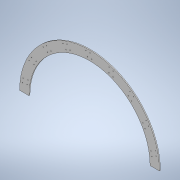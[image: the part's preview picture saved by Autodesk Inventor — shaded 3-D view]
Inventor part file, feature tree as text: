
AUTODESK INVENTOR PART (.ipt)
format: ipt  version: 2020.3 (Build 243373000, 373)  size: 176,640 bytes
history: native  units: mm
features: extrude x3, sketch x3, pattern_circular x1
ambient origin geometry x8: Origin, YZ Plane, XZ Plane, XY Plane, X Axis, Y Axis, Z Axis, Center Point
bodies: Solid1 (feature_tree)
feature tree (7):
  extrude  "Extrusion1"  Depth=40.0mm
  extrude  "Extrusion2"  Depth=10.0mm TaperAngle=0.0deg
  extrude  "Extrusion3"  Depth=3.0mm
  pattern_circular  "Circular Pattern1"  Count=27  [1 undecoded]
  sketch  "Sketch1"  dims[d0=600.0mm d1=40.0mm]
  sketch  "Sketch2"  dims[d2=4.0mm d3=0.0mm d4=10.0mm d5=0.0mm]
  sketch  "Sketch3"  dims[d6=3.0mm d7=3.0mm d9=270.0mm d11=3.0mm d12=3.0mm d14=270.0mm d16=0.0mm d17=0.0mm d18=90.0mm d19=27.925268mm d21=19.024089mm d22=20.0mm d23=1.396263mm d24=2.094395mm]
note: 1 required parameter value undecoded (feature->parameter linkage not recoverable at this tier; creation-order binding heuristic only, values carry confidence <= 0.55)
